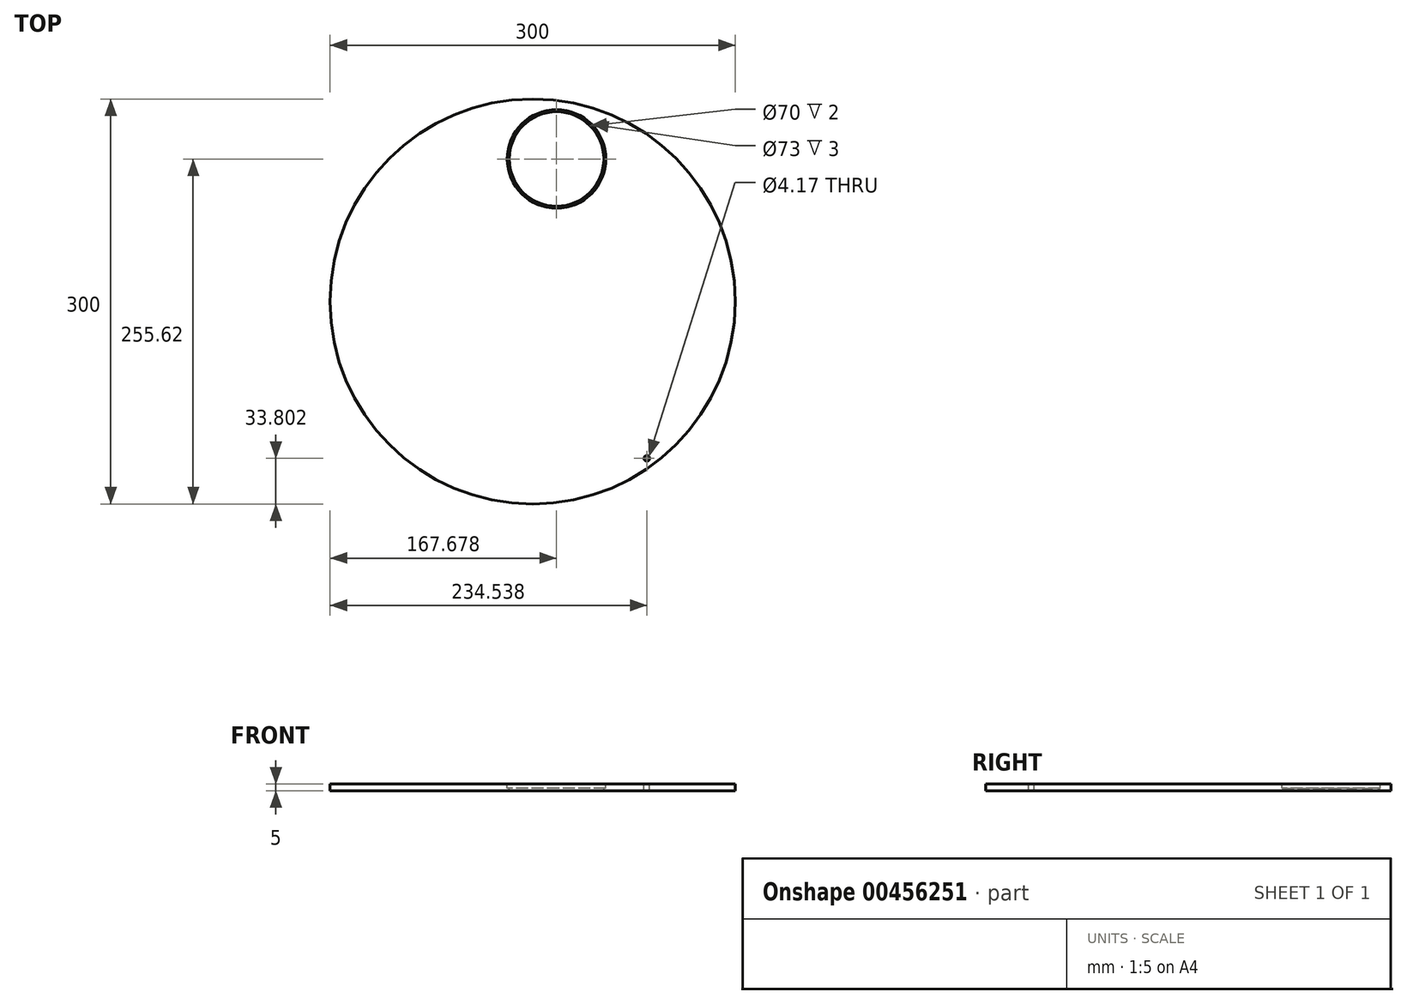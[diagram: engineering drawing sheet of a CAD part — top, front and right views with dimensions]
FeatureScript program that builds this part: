
annotation { "Feature Type Name" : "Feature", "Feature Type Description" : "" }
export const myFeature = defineFeature(function(context is Context, id is Id, definition is map)
    precondition{}
    {
        {
            var Q0;
            Q0=qCreatedBy(makeId("Top.planeOp"),FACE);
            var sketch = newSketch(context, id + "F0", { "sketchPlane" : qUnion([Q0])});
            skCircle(sketch, "E0", {"center": v(0, 0) * mm, "radius": 150 * mm});
            skSolve(sketch);
        }
        {
            var Q0;
            Q0=makeQuery(id+"F0.imprint","IMPRINT",FACE,{"disambiguationData":[TD([[makeQuery(id+"F0.imprint","IMPRINT",EDGE,{"derivedFrom":sQuery(id+"F0.wireOp",EDGE,"E0")}),1.0]])]});
            extrude(context, id + "F1", {"entities" : qUnion([Q0]), "endBound" : BoundingType.SYMMETRIC, "depth" : 5 * mm});
        }
        {
            var Q0;
            Q0=makeQuery(id+"F1.opExtrude","CAP_FACE",FACE,{"disambiguationData":[OSD([sQuery(id+"F0.wireOp",EDGE,"E0")])],"isStart":false});
            var sketch = newSketch(context, id + "F2", { "sketchPlane" : qUnion([Q0])});
            skCircle(sketch, "E1", {"center": v(17.68, 105.62) * mm, "radius": 36.5 * mm});
            skCircle(sketch, "E2", {"center": v(0, 0) * mm, "radius": 107.5 * mm, "construction": true});
            skCircle(sketch, "E3", {"center": v(17.68, 105.62) * mm, "radius": 35 * mm});
            skSolve(sketch);
        }
        {
            var Q0;
            Q0=makeQuery(id+"F2.imprint","IMPRINT",FACE,{"disambiguationData":[TD([[makeQuery(id+"F2.imprint","IMPRINT",EDGE,{"derivedFrom":sQuery(id+"F2.wireOp",EDGE,"E3")}),1.0]])]});
            extrude(context, id + "F3", {"entities" : qUnion([Q0]), "operationType" : NewBodyOperationType.REMOVE, "endBound" : BoundingType.THROUGH_ALL, "oppositeDirection" : true, "depth" : 25 * mm});
        }
        {
            var Q0;
            Q0=makeQuery(id+"F2.imprint","IMPRINT",FACE,{"disambiguationData":[TD([[makeQuery(id+"F2.imprint","IMPRINT",EDGE,{"derivedFrom":sQuery(id+"F2.wireOp",EDGE,"E1")}),1.0]])]});
            extrude(context, id + "F4", {"entities" : qUnion([Q0]), "operationType" : NewBodyOperationType.REMOVE, "oppositeDirection" : true, "depth" : 3 * mm});
        }
        {
            var Q0;
            Q0=makeQuery(id+"F2.imprint","IMPRINT",FACE,{"disambiguationData":[TD([[makeQuery(id+"F2.imprint","IMPRINT",EDGE,{"derivedFrom":sQuery(id+"F2.wireOp",EDGE,"E1")}),-1.0]])]});
            var sketch = newSketch(context, id + "F5", { "sketchPlane" : qUnion([Q0])});
            skCircle(sketch, "E4", {"center": v(84.54, -116.2) * mm, "radius": 2.09 * mm});
            skSolve(sketch);
        }
        {
            var Q0;
            Q0=qSketchRegion(id+"F5",true);
            extrude(context, id + "F6", {"entities" : qUnion([Q0]), "operationType" : NewBodyOperationType.REMOVE, "endBound" : BoundingType.THROUGH_ALL, "oppositeDirection" : true, "depth" : 25 * mm});
        }
    });
